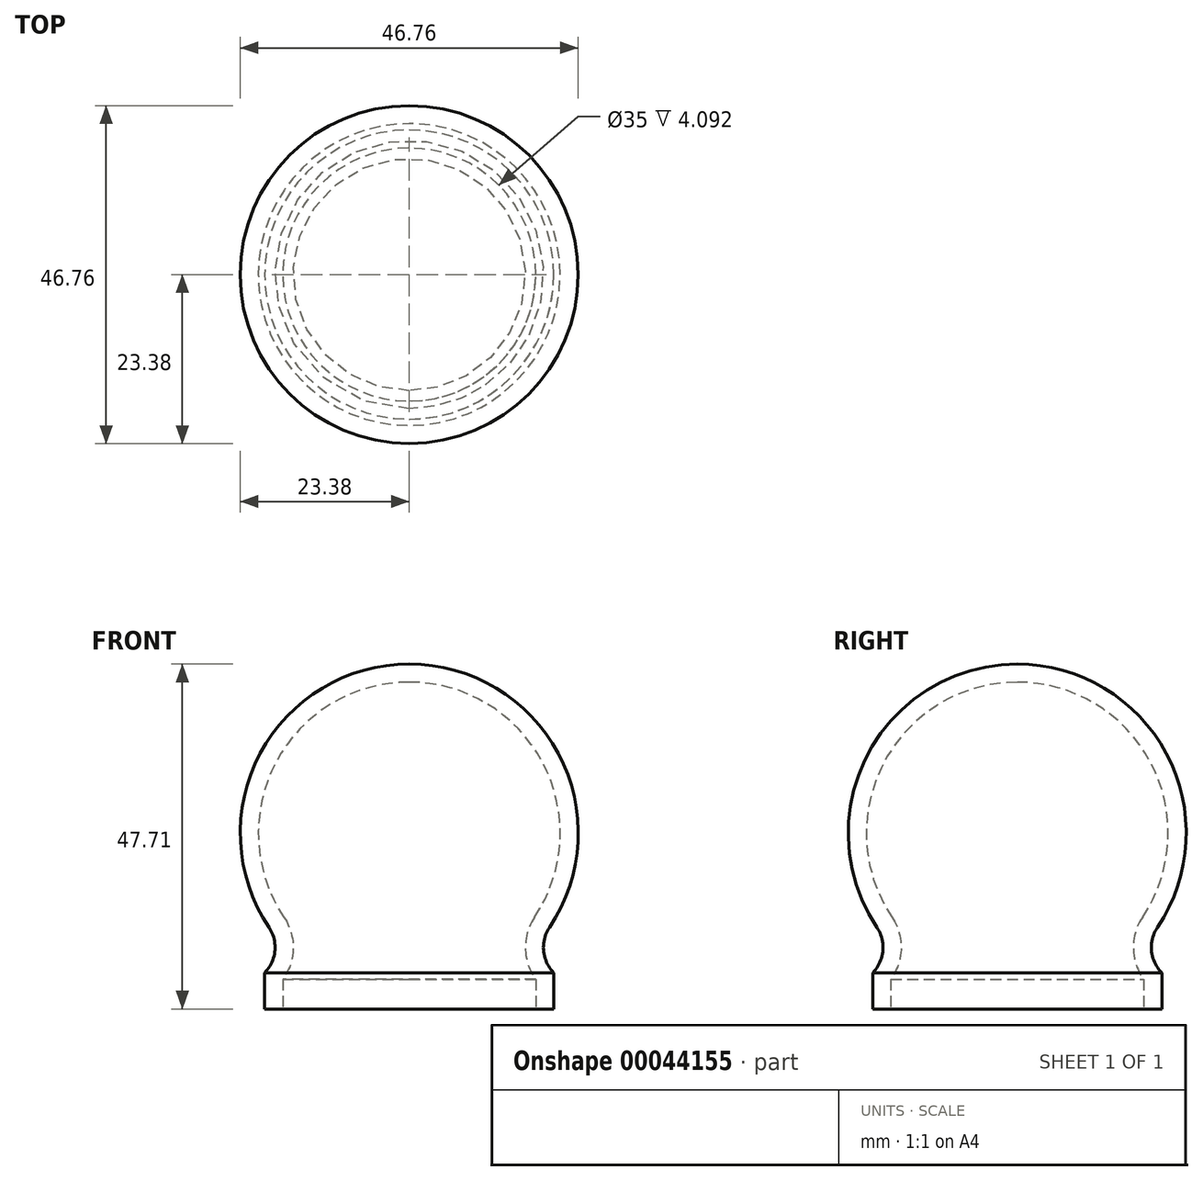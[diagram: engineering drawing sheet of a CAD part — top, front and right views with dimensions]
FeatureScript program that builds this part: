
annotation { "Feature Type Name" : "Feature", "Feature Type Description" : "" }
export const myFeature = defineFeature(function(context is Context, id is Id, definition is map)
    precondition{}
    {
        {
            var Q0;
            Q0=qCreatedBy(makeId("Top.planeOp"),FACE);
            var sketch = newSketch(context, id + "F0", { "sketchPlane" : qUnion([Q0])});
            skCircle(sketch, "E0", {"center": v(0, 0) * mm, "radius": 20 * mm});
            skSolve(sketch);
        }
        {
            var Q0;
            Q0 = qSketchRegion(id + "F0", true);
            extrude(context, id + "F1", {"entities" : qUnion([Q0]), "depth" : 5 * mm});
        }
        {
            var Q0;
            Q0=qCreatedBy(makeId("Right.planeOp"),FACE);
            var sketch = newSketch(context, id + "F2", { "sketchPlane" : qUnion([Q0])});
            skArc(sketch, "E1", {"start": v(0, 47.7) * mm, "mid": v(-23.38, 24.33) * mm, "end": v(0, 0.95) * mm});
            skLineSegment(sketch, "E2", {"start": v(0, 0) * mm, "end": v(0, 47.7) * mm});
            skSolve(sketch);
        }
        {
            var Q0;
            {var subQ0=sQuery(id+"F2.wireOp",EDGE,"E1");Q0=makeQuery(id+"F2.imprint","IMPRINT",FACE,{"disambiguationData":[TD([[makeQuery(id+"F2.imprint","IMPRINT",EDGE,{"derivedFrom":subQ0}),1.0]])]});}
            var Q1;
            Q1=sQuery(id+"F2.wireOp",EDGE,"E2");
            revolve(context, id + "F3", {"operationType" : NewBodyOperationType.ADD, "entities" : qUnion([Q0]), "axis" : qUnion([Q1]), "revolveType" : RevolveType.FULL});
        }
        {
            var Q0;
            Q0=makeQuery(id+"F3.boolean.opBoolean","INTERSECT",EDGE,{"derivedFrom":[makeQuery(id+"F1.opExtrude","CAP_FACE",FACE,{"disambiguationData":[OSD([sQuery(id+"F0.wireOp",EDGE,"E0")])],"isStart":false}),makeQuery(id+"F3.opRevolve","SWEPT_FACE",FACE,{"disambiguationData":[OSD([sQuery(id+"F2.wireOp",EDGE,"E1")])]})]});
            fillet(context, id + "F4", {"entities" : qUnion([Q0]), "radius" : 5 * mm, "tangentPropagation" : true, "allowEdgeOverflow" : false});
        }
        {
            var Q0;
            Q0=makeQuery(id+"F1.opExtrude","CAP_FACE",FACE,{"disambiguationData":[OSD([sQuery(id+"F0.wireOp",EDGE,"E0")])],"isStart":true});
            shell(context, id + "F5", {"entities" : qUnion([Q0]), "thickness" : 2.5 * mm});
        }
    });
